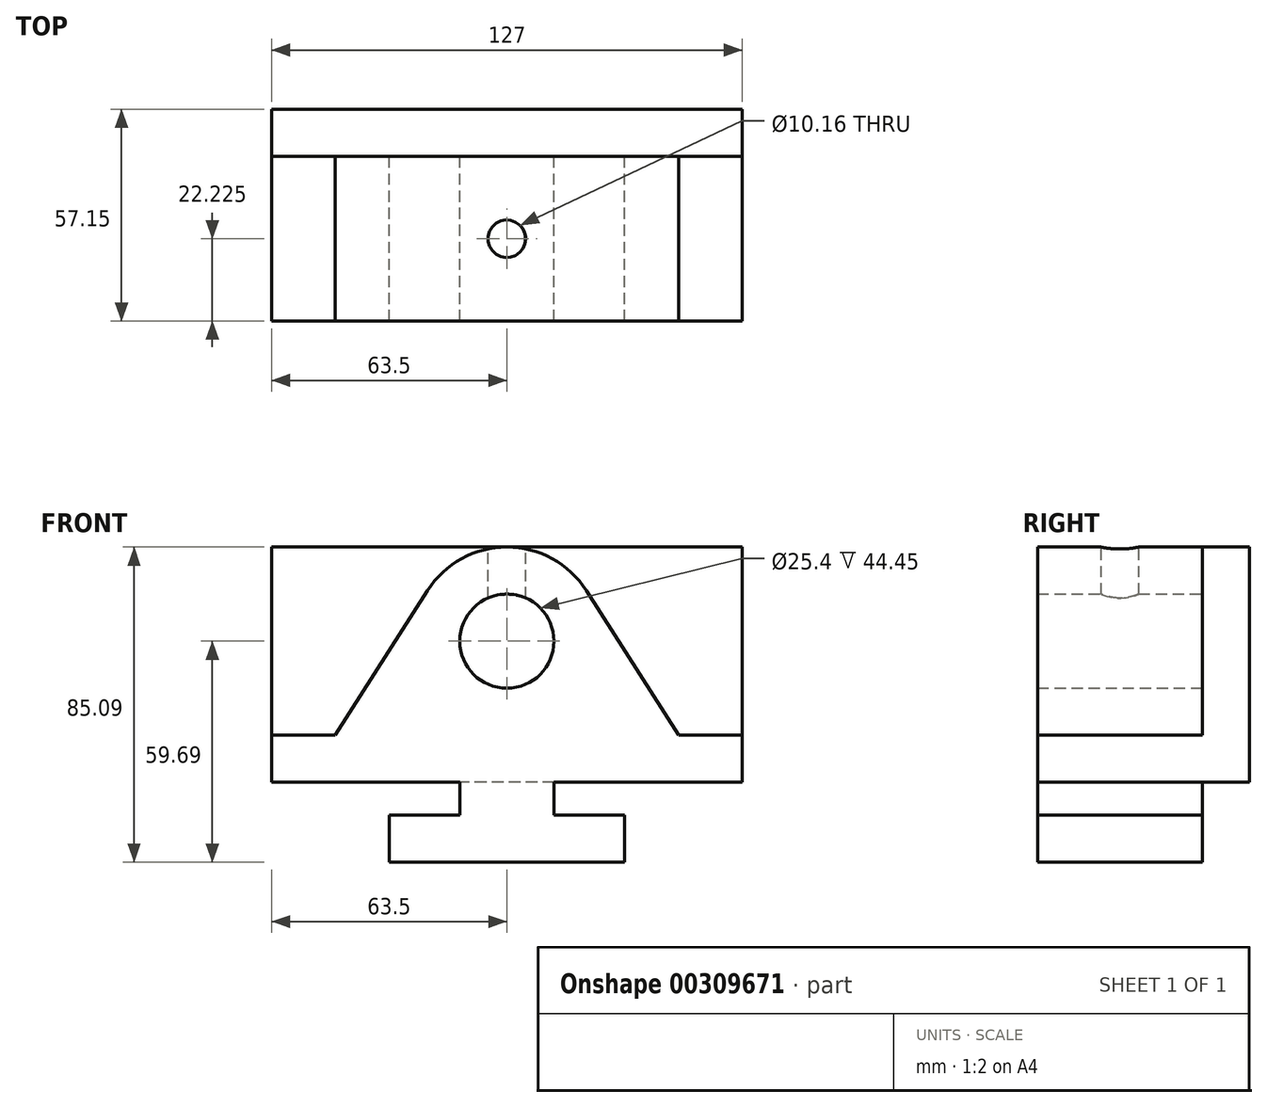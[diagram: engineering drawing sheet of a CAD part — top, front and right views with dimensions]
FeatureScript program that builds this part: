
annotation { "Feature Type Name" : "Feature", "Feature Type Description" : "" }
export const myFeature = defineFeature(function(context is Context, id is Id, definition is map)
    precondition{}
    {
        {
            var Q0;
            Q0=qCreatedBy(makeId("Front.planeOp"),FACE);
            var sketch = newSketch(context, id + "F0", { "sketchPlane" : qUnion([Q0])});
            skLineSegment(sketch, "E0", {"start": v(0, 0) * mm, "end": v(-31.75, 0) * mm});
            skLineSegment(sketch, "E1", {"start": v(-31.75, 0) * mm, "end": v(-31.75, 12.7) * mm});
            skLineSegment(sketch, "E2", {"start": v(-31.75, 12.7) * mm, "end": v(-12.7, 12.7) * mm});
            skLineSegment(sketch, "E3", {"start": v(-12.7, 12.7) * mm, "end": v(-12.7, 21.59) * mm});
            skLineSegment(sketch, "E4", {"start": v(-12.7, 21.59) * mm, "end": v(-63.5, 21.59) * mm});
            skLineSegment(sketch, "E5", {"start": v(-63.5, 21.59) * mm, "end": v(-63.5, 34.29) * mm});
            skLineSegment(sketch, "E6", {"start": v(-63.5, 34.29) * mm, "end": v(-46.35, 34.29) * mm});
            skLineSegment(sketch, "E7", {"start": v(46.35, 34.29) * mm, "end": v(63.5, 34.29) * mm});
            skLineSegment(sketch, "E8", {"start": v(63.5, 34.29) * mm, "end": v(63.5, 21.59) * mm});
            skLineSegment(sketch, "E9", {"start": v(63.5, 21.6) * mm, "end": v(12.7, 21.59) * mm});
            skLineSegment(sketch, "E10", {"start": v(12.7, 21.59) * mm, "end": v(12.7, 12.7) * mm});
            skLineSegment(sketch, "E11", {"start": v(12.7, 12.7) * mm, "end": v(31.75, 12.7) * mm});
            skLineSegment(sketch, "E12", {"start": v(31.75, 12.7) * mm, "end": v(31.75, 0) * mm});
            skLineSegment(sketch, "E13", {"start": v(31.75, 0) * mm, "end": v(0, 0) * mm});
            skLineSegment(sketch, "E14", {"start": v(0, 0) * mm, "end": v(0, 59.7) * mm, "construction": true});
            skLineSegment(sketch, "E15", {"start": v(-46.35, 34.3) * mm, "end": v(-21.4, 73.36) * mm});
            skLineSegment(sketch, "E16", {"start": v(46.35, 34.3) * mm, "end": v(21.4, 73.36) * mm});
            skArc(sketch, "E17", {"start": v(21.4, 73.36) * mm, "mid": v(0, 85.1) * mm, "end": v(-21.4, 73.36) * mm});
            skCircle(sketch, "E18", {"center": v(0, 59.7) * mm, "radius": 12.7 * mm});
            skSolve(sketch);
        }
        {
            var Q0;
            Q0 = qSketchRegion(id + "F0", true);
            extrude(context, id + "F1", {"entities" : qUnion([Q0]), "depth" : 44.45 * mm});
        }
        {
            var Q0;
            Q0=makeQuery(id+"F1.opExtrude","CAP_FACE",FACE,{"disambiguationData":[OSD([sQuery(id+"F0.wireOp",EDGE,"E0"),sQuery(id+"F0.wireOp",EDGE,"E1"),sQuery(id+"F0.wireOp",EDGE,"E2"),sQuery(id+"F0.wireOp",EDGE,"E3"),sQuery(id+"F0.wireOp",EDGE,"E4"),sQuery(id+"F0.wireOp",EDGE,"E5"),sQuery(id+"F0.wireOp",EDGE,"E6"),sQuery(id+"F0.wireOp",EDGE,"E7"),sQuery(id+"F0.wireOp",EDGE,"E8"),sQuery(id+"F0.wireOp",EDGE,"E9"),sQuery(id+"F0.wireOp",EDGE,"E10"),sQuery(id+"F0.wireOp",EDGE,"E11"),sQuery(id+"F0.wireOp",EDGE,"E12"),sQuery(id+"F0.wireOp",EDGE,"E13"),sQuery(id+"F0.wireOp",EDGE,"E15"),sQuery(id+"F0.wireOp",EDGE,"E16"),sQuery(id+"F0.wireOp",EDGE,"E17"),sQuery(id+"F0.wireOp",EDGE,"E18")])],"isStart":true});
            var sketch = newSketch(context, id + "F2", { "sketchPlane" : qUnion([Q0])});
            skLineSegment(sketch, "E19.bottom", {"start": v(-63.5, 21.59) * mm, "end": v(63.5, 21.59) * mm});
            skLineSegment(sketch, "E19.top", {"start": v(-63.5, 85.09) * mm, "end": v(63.5, 85.09) * mm});
            skLineSegment(sketch, "E19.left", {"start": v(-63.5, 21.59) * mm, "end": v(-63.5, 85.09) * mm});
            skLineSegment(sketch, "E19.right", {"start": v(63.5, 21.59) * mm, "end": v(63.5, 85.09) * mm});
            skSolve(sketch);
        }
        {
            var Q0;
            Q0 = qSketchRegion(id + "F2", true);
            extrude(context, id + "F3", {"entities" : qUnion([Q0]), "operationType" : NewBodyOperationType.ADD, "depth" : 12.7 * mm});
        }
        {
            var Q0;
            Q0=qCreatedBy(makeId("Top.planeOp"),FACE);
            cPlane(context, id + "F4", {"entities" : qUnion([Q0]), "cplaneType" : CPlaneType.OFFSET, "offset" : 85.1 * mm, "width" : 152.4 * mm, "height" : 152.4 * mm});
        }
        {
            var Q0;
            Q0=qCreatedBy(id+"F4.planeOp",FACE);
            var sketch = newSketch(context, id + "F5", { "sketchPlane" : qUnion([Q0])});
            skCircle(sketch, "E20", {"center": v(0, -22.23) * mm, "radius": 5.08 * mm});
            skSolve(sketch);
        }
        {
            var Q0;
            Q0 = qSketchRegion(id + "F5", true);
            extrude(context, id + "F6", {"entities" : qUnion([Q0]), "operationType" : NewBodyOperationType.REMOVE, "oppositeDirection" : true, "depth" : 25.4 * mm});
        }
    });
